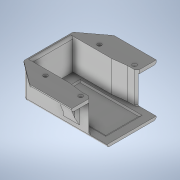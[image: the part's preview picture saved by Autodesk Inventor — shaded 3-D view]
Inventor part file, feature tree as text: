
AUTODESK INVENTOR PART (.ipt)
format: ipt  version: 2022.6 (Build 266554000, 554)  size: 378,368 bytes
history: native  units: mm
features: sketch x10, projected_geometry x9, extrude x8, chamfer x5, fillet x5, plane x4, hole x1, rib x1, mirror x1
ambient origin geometry x8: Origin, YZ Plane, XZ Plane, XY Plane, X Axis, Y Axis, Z Axis, Center Point
bodies: Solid1 (feature_tree)
feature tree (44):
  extrude  "Extrusion1"  Depth=36.0mm
  extrude  "Extrusion2"  Depth=3.0mm
  extrude  "Extrusion4"  Depth=3.0mm
  hole  "Hole1"  [1 undecoded]
  plane  "Work Plane1"
  rib  "Rib1"
  plane  "Work Plane2"
  chamfer  "Chamfer2"  Distance=3.0mm
  mirror  "Mirror2"
  chamfer  "Chamfer3"  Distance=5.0mm
  fillet  "Fillet3"  Radius=40.5mm
  fillet  "Fillet5"  Radius=5.0mm
  fillet  "Fillet6"  Radius=17.0mm
  extrude  "Extrusion5"  Depth=2.0mm TaperAngle=45.0deg
  fillet  "Fillet7"  Radius=2.0mm
  plane  "Work Plane3"
  extrude  "Extrusion6"  Depth=2.0mm
  extrude  "Extrusion8"  Depth=2.0mm
  chamfer  "Chamfer4"  Distance=2.0mm
  extrude  "Extrusion10"  Depth=18.0mm
  chamfer  "Chamfer5"  Distance=25.0mm
  fillet  "Fillet9"  Radius=35.0mm
  plane  "Work Plane4"
  extrude  "Extrusion11"  Depth=0.8mm TaperAngle=0.0deg
  chamfer  "Chamfer6"  Distance=2.0mm
  sketch  "Sketch1"  dims[d0=36.0mm d1=78.0mm]
  sketch  "Sketch2"  dims[d2=2.5mm d3=0.0mm d4=3.0mm]
  sketch  "Sketch3"  dims[d5=3.0mm d6=3.0mm]
  sketch  "Sketch4"  dims[d7=26.5mm d8=2.5mm d9=0.0mm d10=0.0mm d30=15.0mm]
  sketch  "Sketch5"  dims[d31=15.0mm]
  projected_geometry  "Projected Loop1"
  projected_geometry  "Projected Loop2"
  projected_geometry  "Projected Loop3"
  sketch  "Sketch6"  dims[d32=20.0mm d33=3.0mm d34=0.0mm]
  projected_geometry  "Projected Loop4"
  sketch  "Sketch7"  dims[d43=30.0mm]
  projected_geometry  "Projected Loop5"
  projected_geometry  "Projected Loop7"
  projected_geometry  "Projected Loop8"
  sketch  "Sketch9"  dims[d45=20.5mm]
  projected_geometry  "Projected Loop11"
  sketch  "Sketch11"  dims[d47=3.4mm d48=6.0mm d49=4.0mm d50=2.0mm d51=90.0deg d52=8.0mm d53=20.594885mm]
  projected_geometry  "Projected Loop12"
  sketch  "Sketch12"  dims[d56=5.0mm d57=5.0mm d58=40.5mm d60=5.0mm d61=1.0mm d62=10.0mm d63=0.0mm d64=0.0mm d65=1.0mm d66=1.0mm d67=17.0mm d68=2.0mm d69=2.0mm d70=45.0deg d71=2.0mm d72=2.0mm d73=45.0deg d76=2.0mm d78=2.0mm d79=2.0mm d80=18.0mm d81=25.0mm d82=35.0mm d83=0.4mm d84=0.0mm d85=2.0mm d88=10.0mm d89=0.0mm d90=2.0mm d91=0.0mm d96=25.0mm d97=0.0mm d98=0.0mm d99=3.0mm d100=2.0mm d101=45.0deg d106=3.0mm d107=2.5mm d108=1.0mm d109=0.5mm d110=10.0mm d111=3.0mm d112=1.5mm d114=8.0mm d115=20.0mm d116=10.0mm d117=0.0mm d119=2.0mm d120=2.0mm d121=45.0deg d122=1.0mm d123=18.0mm d124=0.8mm d125=28.0mm d126=50.0mm d127=0.0mm d128=1.5mm d129=0.8mm d130=45.0deg d35=0.5mm d36=0.872665mm d77=0.0mm]
note: 1 required parameter value undecoded (feature->parameter linkage not recoverable at this tier; creation-order binding heuristic only, values carry confidence <= 0.55)
